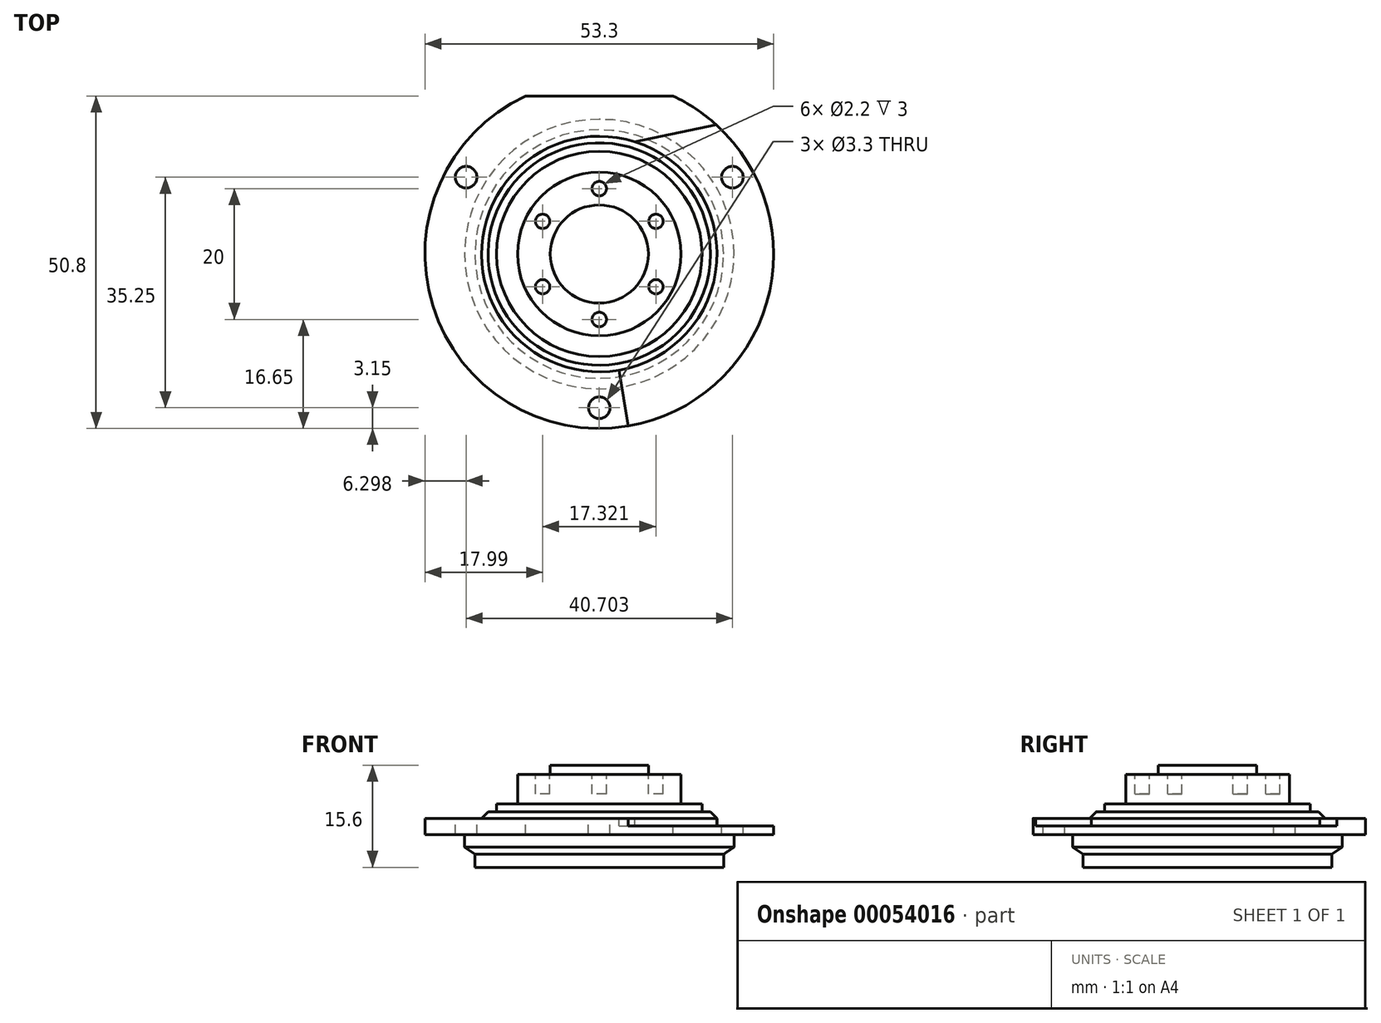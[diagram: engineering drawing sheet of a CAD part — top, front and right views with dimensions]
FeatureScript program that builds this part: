
annotation { "Feature Type Name" : "Feature", "Feature Type Description" : "" }
export const myFeature = defineFeature(function(context is Context, id is Id, definition is map)
    precondition{}
    {
        {
            var Q0;
            Q0=qCreatedBy(makeId("Front.planeOp"),FACE);
            var sketch = newSketch(context, id + "F0", { "sketchPlane" : qUnion([Q0])});
            skLineSegment(sketch, "E0", {"start": v(0, 0) * mm, "end": v(19, 0) * mm});
            skLineSegment(sketch, "E1", {"start": v(19, 0) * mm, "end": v(19, 2) * mm});
            skLineSegment(sketch, "E2", {"start": v(19, 2) * mm, "end": v(20.6, 3.1) * mm});
            skLineSegment(sketch, "E3", {"start": v(20.6, 3.1) * mm, "end": v(20.6, 5) * mm});
            skLineSegment(sketch, "E4", {"start": v(20.6, 5) * mm, "end": v(26.65, 5) * mm});
            skLineSegment(sketch, "E5", {"start": v(26.65, 5) * mm, "end": v(26.65, 7.5) * mm});
            skLineSegment(sketch, "E6", {"start": v(26.65, 7.5) * mm, "end": v(18, 7.5) * mm});
            skLineSegment(sketch, "E7", {"start": v(18, 7.5) * mm, "end": v(17, 8.5) * mm});
            skLineSegment(sketch, "E8", {"start": v(17, 8.5) * mm, "end": v(15.7, 8.5) * mm});
            skLineSegment(sketch, "E9", {"start": v(15.7, 8.5) * mm, "end": v(15.7, 9.7) * mm});
            skLineSegment(sketch, "E10", {"start": v(15.7, 9.7) * mm, "end": v(12.5, 9.7) * mm});
            skLineSegment(sketch, "E11", {"start": v(12.5, 9.7) * mm, "end": v(12.5, 14.2) * mm});
            skLineSegment(sketch, "E12", {"start": v(12.5, 14.2) * mm, "end": v(7.5, 14.2) * mm});
            skLineSegment(sketch, "E13", {"start": v(7.5, 14.2) * mm, "end": v(7.5, 15.6) * mm});
            skLineSegment(sketch, "E14", {"start": v(7.5, 15.6) * mm, "end": v(0, 15.6) * mm});
            skLineSegment(sketch, "E15", {"start": v(0, 15.6) * mm, "end": v(0, 0) * mm});
            skLineSegment(sketch, "E16", {"start": v(0, 0) * mm, "end": v(0, -8.23) * mm, "construction": true});
            skSolve(sketch);
        }
        {
            var Q0;
            Q0 = qSketchRegion(id + "F0", true);
            var Q1;
            Q1=sQuery(id+"F0.wireOp",EDGE,"E16");
            revolve(context, id + "F1", {"entities" : qUnion([Q0]), "axis" : qUnion([Q1]), "revolveType" : RevolveType.FULL});
        }
        {
            var Q0;
            Q0=makeQuery(id+"F1.opRevolve","SWEPT_FACE",FACE,{"disambiguationData":[OSD([sQuery(id+"F0.wireOp",EDGE,"E6")])]});
            var sketch = newSketch(context, id + "F2", { "sketchPlane" : qUnion([Q0])});
            skLineSegment(sketch, "E17", {"start": v(5.41, 17.17) * mm, "end": v(17.86, 19.78) * mm});
            skArc(sketch, "E18", {"start": v(3, -17.75) * mm, "mid": v(17.96, -1.24) * mm, "end": v(5.41, 17.17) * mm});
            skArc(sketch, "E19", {"start": v(4.43, -26.28) * mm, "mid": v(25.58, -7.46) * mm, "end": v(17.86, 19.78) * mm});
            skLineSegment(sketch, "E20", {"start": v(3, -17.75) * mm, "end": v(4.43, -26.28) * mm});
            skSolve(sketch);
        }
        {
            var Q0;
            Q0 = qSketchRegion(id + "F2", true);
            extrude(context, id + "F3", {"entities" : qUnion([Q0]), "operationType" : NewBodyOperationType.REMOVE, "oppositeDirection" : true, "depth" : 1.2 * mm});
        }
        {
            var Q0;
            Q0=makeQuery(id+"F1.opRevolve","SWEPT_FACE",FACE,{"disambiguationData":[OSD([sQuery(id+"F0.wireOp",EDGE,"E12")])]});
            var sketch = newSketch(context, id + "F4", { "sketchPlane" : qUnion([Q0])});
            skCircle(sketch, "E21", {"center": v(0, 10) * mm, "radius": 1.1 * mm});
            skLineSegment(sketch, "E22", {"start": v(0, 12.5) * mm, "end": v(0, 7.5) * mm, "construction": true});
            skCircle(sketch, "E23.1.0", {"center": v(-8.66, 5) * mm, "radius": 1.1 * mm});
            skCircle(sketch, "E23.2.0", {"center": v(-8.66, -5) * mm, "radius": 1.1 * mm});
            skPoint(sketch, "E23.center", {"position": v(0, 0) * mm});
            skLineSegment(sketch, "E23.anchor1", {"start": v(0, 0) * mm, "end": v(0, 10) * mm, "construction": true});
            skLineSegment(sketch, "E23.anchor2", {"start": v(0, 0) * mm, "end": v(8.66, 5) * mm, "construction": true});
            skCircle(sketch, "E24.1.3.0", {"center": v(0, -10) * mm, "radius": 1.1 * mm});
            skCircle(sketch, "E24.1.4.0", {"center": v(8.66, -5) * mm, "radius": 1.1 * mm});
            skCircle(sketch, "E24.1.5.0", {"center": v(8.66, 5) * mm, "radius": 1.1 * mm});
            skSolve(sketch);
        }
        {
            var Q0;
            Q0 = qSketchRegion(id + "F4", true);
            extrude(context, id + "F5", {"entities" : qUnion([Q0]), "operationType" : NewBodyOperationType.REMOVE, "oppositeDirection" : true, "depth" : 3 * mm});
        }
        {
            var Q0;
            Q0=makeQuery(id+"F1.opRevolve","SWEPT_FACE",FACE,{"disambiguationData":[OSD([sQuery(id+"F0.wireOp",EDGE,"E6")])]});
            var sketch = newSketch(context, id + "F6", { "sketchPlane" : qUnion([Q0])});
            skLineSegment(sketch, "E25", {"start": v(-11.27, 24.15) * mm, "end": v(11.27, 24.15) * mm});
            skArc(sketch, "E26", {"start": v(11.27, 24.15) * mm, "mid": v(0, 26.65) * mm, "end": v(-11.27, 24.15) * mm});
            skLineSegment(sketch, "E27", {"start": v(0, -26.65) * mm, "end": v(0, -18) * mm, "construction": true});
            skCircle(sketch, "E28", {"center": v(0, -23.5) * mm, "radius": 1.65 * mm});
            skCircle(sketch, "E29.1.0", {"center": v(20.35, 11.75) * mm, "radius": 1.65 * mm});
            skCircle(sketch, "E29.2.0", {"center": v(-20.35, 11.75) * mm, "radius": 1.65 * mm});
            skSolve(sketch);
        }
        {
            var Q0;
            Q0 = qSketchRegion(id + "F6", true);
            extrude(context, id + "F7", {"entities" : qUnion([Q0]), "operationType" : NewBodyOperationType.REMOVE, "endBound" : BoundingType.THROUGH_ALL, "oppositeDirection" : true, "depth" : 25 * mm});
        }
    });
